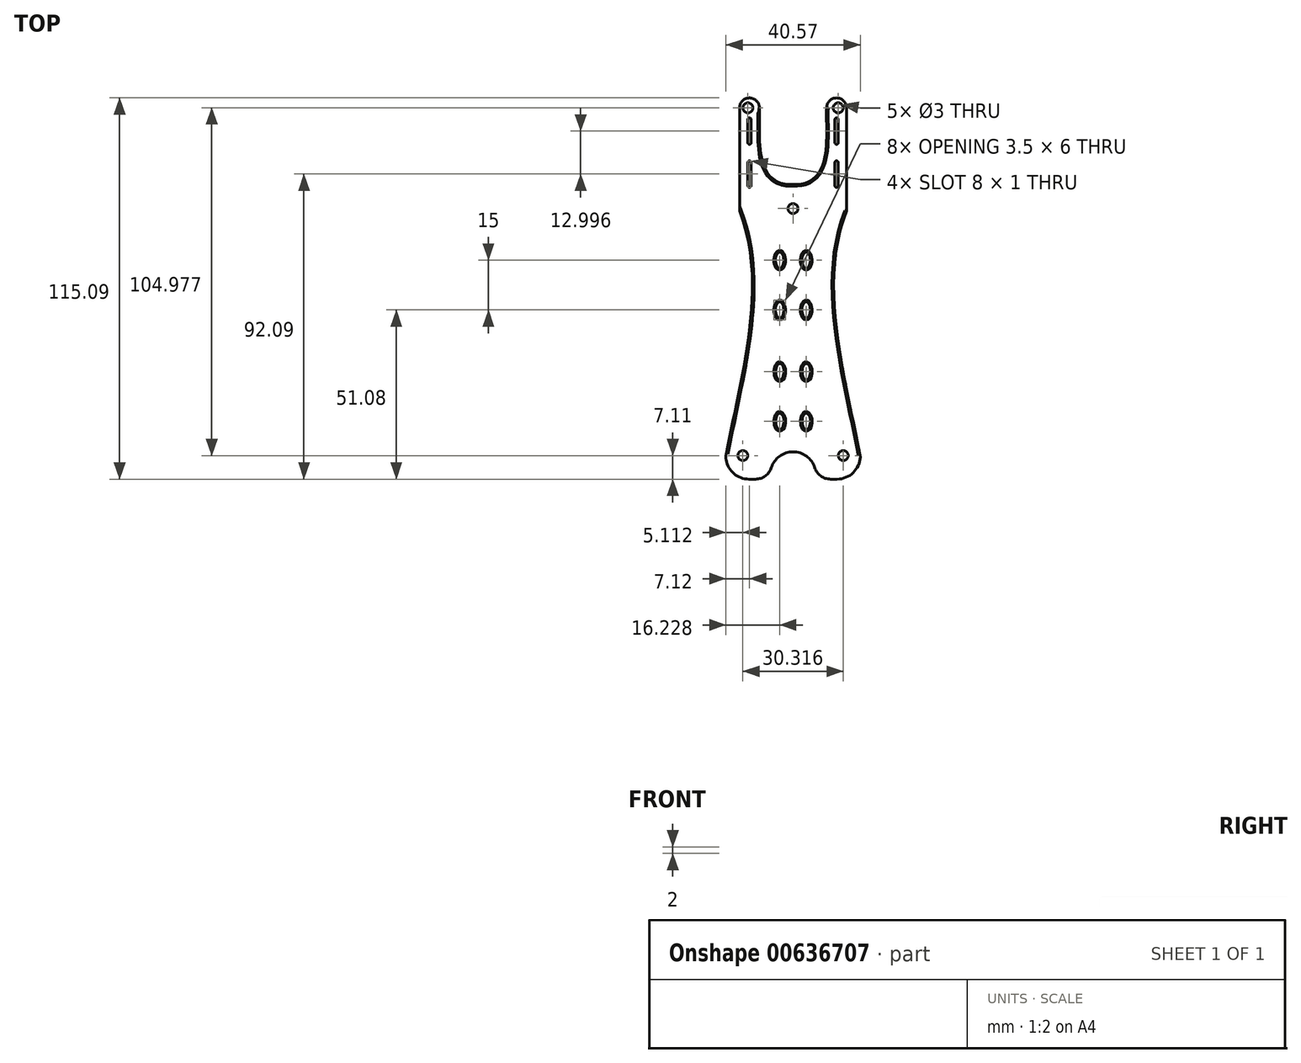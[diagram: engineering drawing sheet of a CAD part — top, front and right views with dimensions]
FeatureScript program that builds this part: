
annotation { "Feature Type Name" : "Feature", "Feature Type Description" : "" }
export const myFeature = defineFeature(function(context is Context, id is Id, definition is map)
    precondition{}
    {
        {
            var Q0;
            Q0=qCreatedBy(makeId("Top.planeOp"),FACE);
            var sketch = newSketch(context, id + "F0", { "sketchPlane" : qUnion([Q0])});
            skLineSegment(sketch, "E0", {"start": v(16.15, 29.9) * mm, "end": v(16.15, 61) * mm});
            skPoint(sketch, "E1.visualSharp", {"position": v(16.15, 66) * mm});
            skArc(sketch, "E1.filletArc", {"start": v(16.15, 61) * mm, "mid": v(15.24, 63.16) * mm, "end": v(13.06, 64) * mm});
            skArc(sketch, "E2", {"start": v(13.65, 57.5) * mm, "mid": v(13.11, 58) * mm, "end": v(12.65, 57.44) * mm});
            skArc(sketch, "E3", {"start": v(12.65, 37.58) * mm, "mid": v(13.11, 37.01) * mm, "end": v(13.65, 37.5) * mm});
            skLineSegment(sketch, "E4", {"start": v(13.65, 57.5) * mm, "end": v(13.65, 50.5) * mm});
            skLineSegment(sketch, "E5", {"start": v(12.65, 57.57) * mm, "end": v(12.65, 50.44) * mm});
            skPoint(sketch, "E6.visualSharp", {"position": v(8.63, 59.12) * mm});
            skPoint(sketch, "E7.visualSharp", {"position": v(8.63, 31.4) * mm});
            skCircle(sketch, "E8.MirrorC", {"center": v(13.63, 61) * mm, "radius": 1.5 * mm});
            skArc(sketch, "E9", {"start": v(12.65, 50.57) * mm, "mid": v(13.11, 50) * mm, "end": v(13.65, 50.5) * mm});
            skArc(sketch, "E10", {"start": v(13.65, 44.5) * mm, "mid": v(13.11, 45) * mm, "end": v(12.65, 44.44) * mm});
            skLineSegment(sketch, "E11.trimOffspring", {"start": v(12.65, 44.58) * mm, "end": v(12.65, 37.44) * mm});
            skLineSegment(sketch, "E12.trimOffspring", {"start": v(13.65, 44.5) * mm, "end": v(13.65, 37.5) * mm});
            skCircle(sketch, "E13", {"center": v(0, 30.6) * mm, "radius": 1.5 * mm});
            skCircle(sketch, "E14", {"center": v(15.16, -43.97) * mm, "radius": 1.5 * mm});
            skArc(sketch, "E15", {"start": v(13.06, 64) * mm, "mid": v(11, 63.1) * mm, "end": v(10.15, 61) * mm});
            skFitSpline(sketch, "E16", {"points": [v(10.15, 61) * mm, v(0, 37.84) * mm], "startDerivative": vector(-1.26, -21.95) * mm, "endDerivative": vector(-37.96, 1.2) * mm});
            skArc(sketch, "E17.MirrorCS", {"start": v(-12.65, 50.57) * mm, "mid": v(-13.11, 50) * mm, "end": v(-13.65, 50.5) * mm});
            skArc(sketch, "E18.MirrorCS", {"start": v(-13.65, 57.5) * mm, "mid": v(-13.11, 58) * mm, "end": v(-12.65, 57.44) * mm});
            skLineSegment(sketch, "E19.MirrorCS", {"start": v(-13.65, 57.5) * mm, "end": v(-13.65, 50.5) * mm});
            skCircle(sketch, "E20.MirrorC", {"center": v(-13.63, 61) * mm, "radius": 1.5 * mm});
            skLineSegment(sketch, "E21.MirrorCS", {"start": v(-12.65, 57.57) * mm, "end": v(-12.65, 50.44) * mm});
            skArc(sketch, "E22.MirrorCS", {"start": v(-16.15, 61) * mm, "mid": v(-15.24, 63.16) * mm, "end": v(-13.06, 64) * mm});
            skCircle(sketch, "E23.MirrorC", {"center": v(-15.16, -43.97) * mm, "radius": 1.5 * mm});
            skLineSegment(sketch, "E24.MirrorCS", {"start": v(-16.15, 29.9) * mm, "end": v(-16.15, 61) * mm});
            skArc(sketch, "E25.MirrorCS", {"start": v(-13.06, 64) * mm, "mid": v(-11, 63.1) * mm, "end": v(-10.15, 61) * mm});
            skPoint(sketch, "E26.MirrorP", {"position": v(-16.15, 66) * mm});
            skPoint(sketch, "E27.MirrorP", {"position": v(-8.63, 31.4) * mm});
            skFitSpline(sketch, "E28.MirrorCS", {"points": [v(-10.15, 61) * mm, v(0, 37.84) * mm], "startDerivative": vector(1.26, -21.95) * mm, "endDerivative": vector(37.96, 1.2) * mm});
            skPoint(sketch, "E29.MirrorP", {"position": v(-8.63, 59.12) * mm});
            skEllipse(sketch, "E30", {"center": v(-4, -33.64) * mm, "majorRadius": 2.5 * mm, "minorRadius": 1.25 * mm, "majorAxis": v(0, -1)});
            skEllipse(sketch, "E31", {"center": v(-4, -18.64) * mm, "majorRadius": 2.5 * mm, "minorRadius": 1.25 * mm, "majorAxis": v(0, -1)});
            skEllipse(sketch, "E32.MirrorC", {"center": v(4, -18.64) * mm, "majorRadius": 2.5 * mm, "minorRadius": 1.25 * mm, "majorAxis": v(0, -1)});
            skEllipse(sketch, "E33.MirrorC", {"center": v(4, -33.64) * mm, "majorRadius": 2.5 * mm, "minorRadius": 1.25 * mm, "majorAxis": v(0, -1)});
            skLineSegment(sketch, "E34.MirrorCS", {"start": v(-12.65, 44.58) * mm, "end": v(-12.65, 37.44) * mm});
            skLineSegment(sketch, "E35.MirrorCS", {"start": v(-13.65, 44.5) * mm, "end": v(-13.65, 37.5) * mm});
            skArc(sketch, "E36.MirrorCS", {"start": v(-12.65, 37.58) * mm, "mid": v(-13.11, 37.01) * mm, "end": v(-13.65, 37.5) * mm});
            skArc(sketch, "E37.MirrorCS", {"start": v(-13.65, 44.5) * mm, "mid": v(-13.11, 45) * mm, "end": v(-12.65, 44.44) * mm});
            skArc(sketch, "E38", {"start": v(6.55, -47.6) * mm, "mid": v(0, -42.82) * mm, "end": v(-6.55, -47.6) * mm});
            skLineSegment(sketch, "E39", {"start": v(-13.3, -51.08) * mm, "end": v(-11.32, -51.08) * mm});
            skLineSegment(sketch, "E40", {"start": v(11.32, -51.08) * mm, "end": v(13.3, -51.08) * mm});
            skPoint(sketch, "E41.visualSharp", {"position": v(-6.74, -51.08) * mm});
            skArc(sketch, "E41.filletArc", {"start": v(-11.32, -51.08) * mm, "mid": v(-8.37, -50.12) * mm, "end": v(-6.55, -47.6) * mm});
            skPoint(sketch, "E42.visualSharp", {"position": v(6.74, -51.08) * mm});
            skArc(sketch, "E42.filletArc", {"start": v(6.55, -47.6) * mm, "mid": v(8.37, -50.12) * mm, "end": v(11.32, -51.08) * mm});
            skPoint(sketch, "E43.visualSharp", {"position": v(18.3, -51.08) * mm});
            skArc(sketch, "E43.filletArc", {"start": v(13.3, -51.08) * mm, "mid": v(18.16, -49.12) * mm, "end": v(20.3, -44.34) * mm});
            skPoint(sketch, "E44.visualSharp", {"position": v(-18.3, -51.08) * mm});
            skArc(sketch, "E44.filletArc", {"start": v(-20.2, -45.28) * mm, "mid": v(-17.8, -49.44) * mm, "end": v(-13.3, -51.08) * mm});
            skFitSpline(sketch, "E45", {"points": [v(16.15, 29.9) * mm, v(20.3, -44.08) * mm], "startDerivative": vector(-25.7, -65.47) * mm, "endDerivative": vector(15.54, -78.47) * mm});
            skFitSpline(sketch, "E46.MirrorCS", {"points": [v(-16.15, 29.9) * mm, v(-20.3, -44.08) * mm], "startDerivative": vector(25.7, -65.47) * mm, "endDerivative": vector(-15.54, -78.47) * mm});
            skEllipse(sketch, "E47", {"center": v(-4.04, 0) * mm, "majorRadius": 2.5 * mm, "minorRadius": 1.25 * mm, "majorAxis": v(0, -1)});
            skEllipse(sketch, "E48", {"center": v(-4.04, 15) * mm, "majorRadius": 2.5 * mm, "minorRadius": 1.25 * mm, "majorAxis": v(0, -1)});
            skEllipse(sketch, "E49.MirrorC", {"center": v(3.96, 15) * mm, "majorRadius": 2.5 * mm, "minorRadius": 1.25 * mm, "majorAxis": v(0, -1)});
            skEllipse(sketch, "E50.MirrorC", {"center": v(3.96, 0) * mm, "majorRadius": 2.5 * mm, "minorRadius": 1.25 * mm, "majorAxis": v(0, -1)});
            skArc(sketch, "E51.filletArc", {"start": v(-20.17, -43.45) * mm, "mid": v(-20.27, -44.36) * mm, "end": v(-20.2, -45.28) * mm});
            skArc(sketch, "E52.filletArc", {"start": v(20.3, -44.34) * mm, "mid": v(20.3, -44.1) * mm, "end": v(20.26, -43.87) * mm});
            skLineSegment(sketch, "E53", {"start": v(-16.15, 29.9) * mm, "end": v(-16.15, 29.9) * mm});
            skSolve(sketch);
        }
        {
            var Q0;
            Q0=makeQuery(id+"F0.imprint","IMPRINT",FACE,{"disambiguationData":[TD([[makeQuery(id+"F0.imprint","IMPRINT",EDGE,{"derivedFrom":sQuery(id+"F0.wireOp",EDGE,"E0")}),1.0]])]});
            extrude(context, id + "F1", {"entities" : qUnion([Q0]), "depth" : 2 * mm, "offsetDistance" : 25 * mm});
        }
        {
            var Q0;
            Q0=makeQuery(id+"F1.opExtrude","CAP_EDGE",EDGE,{"disambiguationData":[OSD([sQuery(id+"F0.wireOp",EDGE,"E16")])],"isStart":false});
            var Q1;
            Q1=makeQuery(id+"F1.opExtrude","CAP_EDGE",EDGE,{"disambiguationData":[OSD([sQuery(id+"F0.wireOp",EDGE,"E28.MirrorCS")])],"isStart":false});
            var Q2;
            Q2=makeQuery(id+"F1.opExtrude","CAP_EDGE",EDGE,{"disambiguationData":[OSD([sQuery(id+"F0.wireOp",EDGE,"E1.filletArc"),sQuery(id+"F0.wireOp",EDGE,"E15")])],"isStart":false});
            var Q3;
            Q3=makeQuery(id+"F1.opExtrude","CAP_EDGE",EDGE,{"disambiguationData":[OSD([sQuery(id+"F0.wireOp",EDGE,"E45")])],"isStart":false});
            var Q4;
            Q4=makeQuery(id+"F1.opExtrude","CAP_EDGE",EDGE,{"disambiguationData":[OSD([sQuery(id+"F0.wireOp",EDGE,"E13")])],"isStart":false});
            var Q5;
            Q5=makeQuery(id+"F1.opExtrude","CAP_EDGE",EDGE,{"disambiguationData":[OSD([sQuery(id+"F0.wireOp",EDGE,"E20.MirrorC")])],"isStart":false});
            var Q6;
            Q6=makeQuery(id+"F1.opExtrude","CAP_EDGE",EDGE,{"disambiguationData":[OSD([sQuery(id+"F0.wireOp",EDGE,"E8.MirrorC")])],"isStart":false});
            var Q7;
            Q7=makeQuery(id+"F1.opExtrude","CAP_EDGE",EDGE,{"disambiguationData":[OSD([sQuery(id+"F0.wireOp",EDGE,"E49.MirrorC")])],"isStart":false});
            var Q8;
            Q8=makeQuery(id+"F1.opExtrude","CAP_EDGE",EDGE,{"disambiguationData":[OSD([sQuery(id+"F0.wireOp",EDGE,"E48")])],"isStart":false});
            var Q9;
            Q9=makeQuery(id+"F1.opExtrude","CAP_EDGE",EDGE,{"disambiguationData":[OSD([sQuery(id+"F0.wireOp",EDGE,"E47")])],"isStart":false});
            var Q10;
            Q10=makeQuery(id+"F1.opExtrude","CAP_EDGE",EDGE,{"disambiguationData":[OSD([sQuery(id+"F0.wireOp",EDGE,"E50.MirrorC")])],"isStart":false});
            var Q11;
            Q11=makeQuery(id+"F1.opExtrude","CAP_EDGE",EDGE,{"disambiguationData":[OSD([sQuery(id+"F0.wireOp",EDGE,"E31")])],"isStart":false});
            var Q12;
            Q12=makeQuery(id+"F1.opExtrude","CAP_EDGE",EDGE,{"disambiguationData":[OSD([sQuery(id+"F0.wireOp",EDGE,"E32.MirrorC")])],"isStart":false});
            var Q13;
            Q13=makeQuery(id+"F1.opExtrude","CAP_EDGE",EDGE,{"disambiguationData":[OSD([sQuery(id+"F0.wireOp",EDGE,"E30")])],"isStart":false});
            var Q14;
            Q14=makeQuery(id+"F1.opExtrude","CAP_EDGE",EDGE,{"disambiguationData":[OSD([sQuery(id+"F0.wireOp",EDGE,"E33.MirrorC")])],"isStart":false});
            var Q15;
            Q15=makeQuery(id+"F1.opExtrude","CAP_EDGE",EDGE,{"disambiguationData":[OSD([sQuery(id+"F0.wireOp",EDGE,"E48")])],"isStart":true});
            var Q16;
            Q16=makeQuery(id+"F1.opExtrude","CAP_EDGE",EDGE,{"disambiguationData":[OSD([sQuery(id+"F0.wireOp",EDGE,"E47")])],"isStart":true});
            var Q17;
            Q17=makeQuery(id+"F1.opExtrude","CAP_EDGE",EDGE,{"disambiguationData":[OSD([sQuery(id+"F0.wireOp",EDGE,"E31")])],"isStart":true});
            var Q18;
            Q18=makeQuery(id+"F1.opExtrude","CAP_EDGE",EDGE,{"disambiguationData":[OSD([sQuery(id+"F0.wireOp",EDGE,"E50.MirrorC")])],"isStart":true});
            var Q19;
            Q19=makeQuery(id+"F1.opExtrude","CAP_EDGE",EDGE,{"disambiguationData":[OSD([sQuery(id+"F0.wireOp",EDGE,"E49.MirrorC")])],"isStart":true});
            var Q20;
            Q20=makeQuery(id+"F1.opExtrude","CAP_EDGE",EDGE,{"disambiguationData":[OSD([sQuery(id+"F0.wireOp",EDGE,"E32.MirrorC")])],"isStart":true});
            var Q21;
            Q21=makeQuery(id+"F1.opExtrude","CAP_EDGE",EDGE,{"disambiguationData":[OSD([sQuery(id+"F0.wireOp",EDGE,"E33.MirrorC")])],"isStart":true});
            var Q22;
            Q22=makeQuery(id+"F1.opExtrude","CAP_EDGE",EDGE,{"disambiguationData":[OSD([sQuery(id+"F0.wireOp",EDGE,"E30")])],"isStart":true});
            var Q23;
            Q23=makeQuery(id+"F1.opExtrude","CAP_EDGE",EDGE,{"disambiguationData":[OSD([sQuery(id+"F0.wireOp",EDGE,"E38")])],"isStart":true});
            var Q24;
            Q24=makeQuery(id+"F1.opExtrude","CAP_EDGE",EDGE,{"disambiguationData":[OSD([sQuery(id+"F0.wireOp",EDGE,"E40")])],"isStart":true});
            var Q25;
            Q25=makeQuery(id+"F1.opExtrude","CAP_EDGE",EDGE,{"disambiguationData":[OSD([sQuery(id+"F0.wireOp",EDGE,"E24.MirrorCS"),sQuery(id+"F0.wireOp",EDGE,"E53")])],"isStart":true});
            var Q26;
            Q26=makeQuery(id+"F1.opExtrude","CAP_EDGE",EDGE,{"disambiguationData":[OSD([sQuery(id+"F0.wireOp",EDGE,"E22.MirrorCS"),sQuery(id+"F0.wireOp",EDGE,"E25.MirrorCS")])],"isStart":true});
            var Q27;
            Q27=makeQuery(id+"F1.opExtrude","CAP_EDGE",EDGE,{"disambiguationData":[OSD([sQuery(id+"F0.wireOp",EDGE,"E16")])],"isStart":true});
            var Q28;
            Q28=makeQuery(id+"F1.opExtrude","CAP_EDGE",EDGE,{"disambiguationData":[OSD([sQuery(id+"F0.wireOp",EDGE,"E1.filletArc"),sQuery(id+"F0.wireOp",EDGE,"E15")])],"isStart":true});
            var Q29;
            Q29=makeQuery(id+"F1.opExtrude","CAP_EDGE",EDGE,{"disambiguationData":[OSD([sQuery(id+"F0.wireOp",EDGE,"E0")])],"isStart":true});
            fillet(context, id + "F2", {"entities" : qUnion([Q0, Q1, Q2, Q3, Q4, Q5, Q6, Q7, Q8, Q9, Q10, Q11, Q12, Q13, Q14, Q15, Q16, Q17, Q18, Q19, Q20, Q21, Q22, Q23, Q24, Q25, Q26, Q27, Q28, Q29]), "tangentPropagation" : true, "radius" : 0.5 * mm, "defaultsChanged" : false, "vertexSettings" : [], "allowEdgeOverflow" : false});
        }
    });
